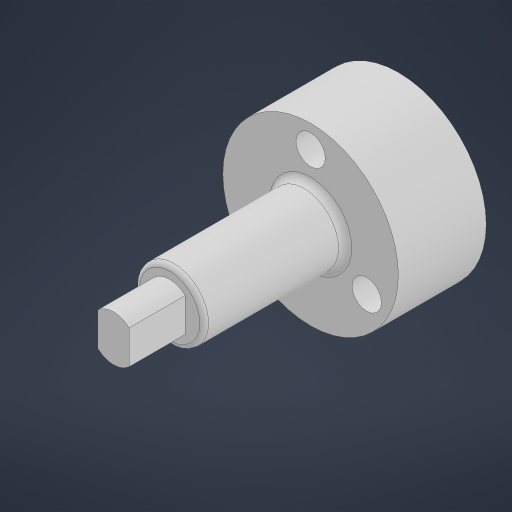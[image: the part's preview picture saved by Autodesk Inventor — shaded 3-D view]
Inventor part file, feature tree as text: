
AUTODESK INVENTOR PART (.ipt)
format: ipt  version: 2023 (Build 270158000, 158)  size: 275,968 bytes
history: native  units: in
note: dims shown in document units (in); Inventor stores cm internally (conversion verified against a paired STEP export)
features: extrude x7, sketch x7, fillet x2, projected_geometry x2
ambient origin geometry x8: Origin, YZ Plane, XZ Plane, XY Plane, X Axis, Y Axis, Z Axis, Center Point
bodies: Solid1 (feature_tree)
feature tree (18):
  extrude  "Extrusion1"  Depth=0.5118in
  extrude  "Extrusion2"  Depth=0.5118in
  extrude  "Extrusion3"  Depth=0.1339in
  extrude  "Extrusion4"  Depth=0.8in
  extrude  "Extrusion5"  Depth=0.2362in
  extrude  "Extrusion6"  Depth=0.315in
  fillet  "Fillet2"  Radius=0.6693in
  extrude  "Extrusion7"  Depth=0.03in TaperAngle=0.0deg
  fillet  "Fillet3"  Radius=0.0016in
  sketch  "Sketch1"  dims[d6=0.5118in d7=0.5118in]
  sketch  "Sketch2"  dims[d8=0.5118in d9=0.4724in]
  projected_geometry  "Projected Loop1"
  sketch  "Sketch3"  dims[d10=0.1339in d11=0.1339in]
  sketch  "Sketch5"  dims[d12=0.1339in d13=0.8in]
  sketch  "Sketch7"  dims[d14=0.1969in d15=0.0in d16=0.2362in]
  sketch  "Sketch8"  dims[d17=0.0787in d18=0.0in d19=0.315in d20=0.6693in d21=0.0in]
  sketch  "Sketch9"  dims[d22=0.2362in d23=0.8932in d24=0.0in d30=0.0016in d31=0.3543in d32=0.0in d33=0.0984in d34=0.0in d36=0.02in d37=0.125in d38=0.0in d39=0.03in d40=0.0in]
  projected_geometry  "Projected Loop2"
